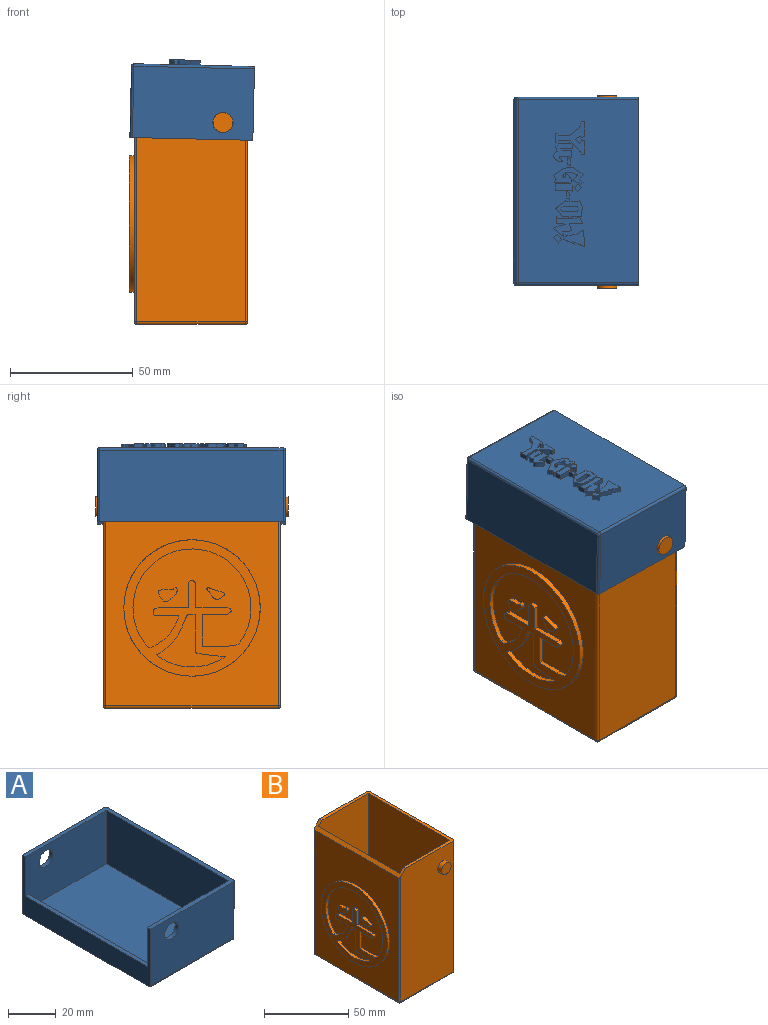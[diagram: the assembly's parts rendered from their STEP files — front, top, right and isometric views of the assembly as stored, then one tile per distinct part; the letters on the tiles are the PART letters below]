
ASSEMBLY  parts=2 mates=1
PART A: 165 faces, bbox 50x76.5x32 mm
  f0: plane 48x27.5mm, normal (0,1,0), area 1252.4mm2, adj f3,f7,f8,f9,f10,f163,f164
  f1: plane 48x27.5mm, normal (0,-1,0), area 1252.4mm2, adj f3,f7,f8,f9,f11,f163,f164
  f2: plane 74.5x49mm, normal (0,0,-1), area 3356mm2, adj f3,f13,f15,f16,f19,f20,f21,f22
  f3: plane 76.5x30mm, normal (-1,0,0), area 835.1mm2, adj f0,f1,f2,f4,f5,f7,f13,f16
  f4: plane 49x29mm, normal (0,1,0), area 1368.2mm2, adj f3,f7,f11,f12,f13
  f5: plane 49x29mm, normal (0,-1,0), area 1368.2mm2, adj f3,f7,f10,f16,f18
  f6: plane 74.5x29mm, normal (1,0,0), area 2160.5mm2, adj f7,f12,f15,f18
  f7: plane 76.5x50mm, normal (0,0,1), area 344.6mm2, adj f0,f1,f3,f4,f5,f6,f8,f12
  f8: plane 72.5x27.5mm, normal (-1,0,0), area 1993.7mm2, adj f0,f1,f7,f9
  f9: plane 72.5x46mm, normal (0,0,1), area 3335mm2, adj f0,f1,f8,f163
  f10: cylinder r=4.1mm len=8.2mm, axis (0,-1,0), area 51.5mm2, adj f0,f5
  f11: cylinder r=4.1mm len=8.2mm, axis (0,1,0), area 51.5mm2, adj f1,f4
  f12: cylinder r=1mm len=29mm, axis (0,0,-1), area 45.6mm2, adj f4,f6,f7,f14
  f13: cylinder r=1mm len=49mm, axis (-1,0,0), area 77mm2, adj f2,f3,f4,f14
  f14: sphere r=1mm, area 1.6mm2, adj f12,f13,f15
  f15: cylinder r=1mm len=74.5mm, axis (0,1,0), area 117mm2, adj f2,f6,f14,f17
  f16: cylinder r=1mm len=49mm, axis (1,0,0), area 77mm2, adj f2,f3,f5,f17
  f17: sphere r=1mm, area 1.6mm2, adj f15,f16,f18
  f18: cylinder r=1mm len=29mm, axis (0,0,1), area 45.6mm2, adj f5,f6,f7,f17
  f19: plane 2x1.25mm, normal (0.04,1,0), area 2.5mm2, adj f2,f20,f45,f46
  f20: plane 2x0.68mm, normal (0.84,0.54,0), area 1.6mm2, adj f2,f19,f21,f46
  f21: plane 2x0.63mm, normal (1,0,0), area 1.3mm2, adj f2,f20,f22,f46
  f22: plane 2x1.26mm, normal (0.91,0.42,0), area 2.8mm2, adj f2,f21,f23,f46
  f23: plane 3.69x3.04mm, normal (0.64,0.77,0), area 9.6mm2, adj f2,f22,f24,f46
  f24: plane 4.67x2mm, normal (0,1,0), area 9.3mm2, adj f2,f23,f25,f46
  f25: plane 2x0.69mm, normal (-0.81,0.58,0), area 1.7mm2, adj f2,f24,f26,f46
  f26: plane 2x0.42mm, normal (0,1,0), area 0.8mm2, adj f2,f25,f27,f46
  f27: plane 3.57x2mm, normal (1,0,0), area 7.1mm2, adj f2,f26,f28,f46
  f28: plane 2x0.42mm, normal (0,-1,0), area 0.8mm2, adj f2,f27,f29,f46
  f29: plane 2x0.73mm, normal (-0.84,-0.54,0), area 1.7mm2, adj f2,f28,f30,f46
  f30: plane 4.93x2mm, normal (0,-1,0), area 9.9mm2, adj f2,f29,f31,f46
  f31: plane 2x1.3mm, normal (0.72,-0.69,0), area 3.6mm2, adj f2,f30,f32,f46
  f32: plane 2x1.64mm, normal (0.72,-0.69,0), area 4.5mm2, adj f2,f31,f33,f46
  f33: plane 2x1.2mm, normal (0.69,-0.72,0), area 3.3mm2, adj f2,f32,f34,f46
  f34: plane 2x1.22mm, normal (0.94,-0.35,0), area 2.6mm2, adj f2,f33,f35,f46
  f35: plane 2x1.15mm, normal (0,-1,0), area 2.3mm2, adj f2,f34,f36,f46
  f36: plane 5.31x2mm, normal (-1,0,0), area 10.6mm2, adj f2,f35,f37,f46
  f37: plane 2x1.15mm, normal (-0.45,0.9,0), area 2.6mm2, adj f2,f36,f38,f46
  f38: plane 2x0.57mm, normal (1,0,0), area 1.1mm2, adj f2,f37,f39,f46
  f39: plane 2x0.84mm, normal (0.72,0.69,0), area 2.3mm2, adj f2,f38,f40,f46
  f40: plane 2x1.72mm, normal (-0.69,0.72,0), area 4.7mm2, adj f2,f39,f41,f46
  f41: plane 2x1.81mm, normal (-0.5,-0.87,0), area 4.2mm2, adj f2,f40,f42,f46
  f42: plane 2x0.31mm, normal (-0.48,-0.88,0), area 0.7mm2, adj f2,f41,f43,f46
  f43: plane 2x0.75mm, normal (0.88,-0.48,0), area 1.7mm2, adj f2,f42,f44,f46
  f44: plane 2x1.25mm, normal (-0.48,-0.88,0), area 2.8mm2, adj f2,f43,f45,f46
  f45: plane 5.87x2mm, normal (-1,0,0), area 11.7mm2, adj f2,f19,f44,f46
  f46: plane 13.11x11.53mm, normal (0,0,-1), area 53.7mm2, adj f19,f20,f21,f22,f23,f24,f25,f26
  f47: extruded ~3.74x3.36mm, area 16.8mm2, adj f2,f48,f61,f62
  f48: plane 4.09x2mm, normal (0,-1,0), area 8.2mm2, adj f2,f47,f49,f62
  f49: plane 2x0.48mm, normal (0.75,-0.66,0), area 1.3mm2, adj f2,f48,f50,f62
  f50: plane 2x0.44mm, normal (0,-1,0), area 0.9mm2, adj f2,f49,f51,f62
  f51: plane 2.96x2mm, normal (-1,0,0), area 5.9mm2, adj f2,f50,f52,f62
  f52: plane 3.77x2mm, normal (0,1,0), area 7.5mm2, adj f2,f51,f53,f62
  f53: plane 2x0.76mm, normal (-0.8,0.6,0), area 1.9mm2, adj f2,f52,f54,f62
  f54: plane 4.52x2mm, normal (0,-1,0), area 9mm2, adj f2,f53,f55,f62
  f55: plane 2x1.47mm, normal (-1,0,0), area 2.9mm2, adj f2,f54,f56,f62
  f56: plane 2x0.91mm, normal (-0.72,0.69,0), area 2.5mm2, adj f2,f55,f57,f62
  f57: plane 2x0.43mm, normal (1,0,0), area 0.9mm2, adj f2,f56,f58,f62
  f58: plane 4.58x2mm, normal (0,1,0), area 9.1mm2, adj f2,f57,f59,f62
  f59: plane 2x1.21mm, normal (0.69,0.72,0), area 3.4mm2, adj f2,f58,f60,f62
  f60: plane 2x1.84mm, normal (0.96,-0.29,0), area 3.9mm2, adj f2,f59,f61,f62
  f61: plane 2x1.07mm, normal (0.69,0.72,0), area 3mm2, adj f2,f47,f60,f62
  f62: plane 7.94x7.77mm, normal (0,0,-1), area 35.4mm2, adj f47,f48,f49,f50,f51,f52,f53,f54
  f63: plane 2x1.33mm, normal (-0.53,0.85,0), area 3.1mm2, adj f2,f64,f66,f67
  f64: plane 2.72x2mm, normal (1,0,0), area 5.4mm2, adj f2,f63,f65,f67
  f65: plane 2x1.33mm, normal (0.34,-0.94,0), area 2.8mm2, adj f2,f64,f66,f67
  f66: plane 2.36x2mm, normal (-1,0,0), area 4.7mm2, adj f2,f63,f65,f67
  f67: plane 3.19x1.33mm, normal (0,0,-1), area 3.4mm2, adj f63,f64,f65,f66
  f68: plane 2x0.41mm, normal (-0.52,-0.85,0), area 1mm2, adj f2,f69,f83,f84
  f69: extruded ~5.78x4.23mm, area 29.1mm2, adj f2,f68,f70,f84
  f70: plane 2x1.78mm, normal (0.81,0.58,0), area 4.4mm2, adj f2,f69,f71,f84
  f71: extruded ~3.12x2mm, area 7.1mm2, adj f2,f70,f72,f84
  f72: plane 2x0.93mm, normal (-0.7,-0.71,0), area 2.6mm2, adj f2,f71,f73,f84
  f73: plane 2x1.33mm, normal (-0.71,0.7,0), area 3.8mm2, adj f2,f72,f74,f84
  f74: plane 2x1.92mm, normal (-0.82,-0.57,0), area 4.7mm2, adj f2,f73,f75,f84
  f75: plane 4.23x2.91mm, normal (-0.57,0.82,0), area 10.3mm2, adj f2,f74,f76,f84
  f76: plane 2.1x2mm, normal (0,1,0), area 4.2mm2, adj f2,f75,f77,f84
  f77: plane 2x1.84mm, normal (0.4,0.91,0), area 4mm2, adj f2,f76,f78,f84
  f78: plane 3.84x2.34mm, normal (0.52,0.85,0), area 9mm2, adj f2,f77,f79,f84
  f79: plane 2x1.66mm, normal (0.85,-0.52,0), area 3.9mm2, adj f2,f78,f80,f84
  f80: plane 2x1.49mm, normal (0.91,0.4,0), area 3.3mm2, adj f2,f79,f81,f84
  f81: plane 5.87x2mm, normal (0,-1,0), area 11.7mm2, adj f2,f80,f82,f84
  f82: plane 2x0.38mm, normal (0.85,-0.52,0), area 0.9mm2, adj f2,f81,f83,f84
  f83: plane 2x0.49mm, normal (-0.26,-0.97,0), area 1mm2, adj f2,f68,f82,f84
  f84: plane 12.01x7.08mm, normal (0,0,-1), area 46.9mm2, adj f68,f69,f70,f71,f72,f73,f74,f75
  f85: plane 2x0.44mm, normal (0.26,0.97,0), area 0.9mm2, adj f2,f86,f96,f97
  f86: plane 4.56x2mm, normal (-0.01,1,0), area 9.1mm2, adj f2,f85,f87,f97
  f87: plane 2x0.48mm, normal (0,1,0), area 1mm2, adj f2,f86,f88,f97
  f88: plane 2.5x2mm, normal (1,0,0), area 5mm2, adj f2,f87,f89,f97
  f89: plane 5.77x2mm, normal (0,-1,0), area 11.5mm2, adj f2,f88,f90,f97
  f90: plane 2x0.85mm, normal (0.5,-0.87,0), area 2mm2, adj f2,f89,f91,f97
  f91: plane 2.48x2mm, normal (-1,0,0), area 5mm2, adj f2,f90,f92,f97
  f92: plane 2x0.72mm, normal (-0.76,0.65,0), area 1.9mm2, adj f2,f91,f93,f97
  f93: plane 2x0.02mm, normal (-0.11,0.99,0), area 0mm2, adj f2,f92,f94,f97
  f94: plane 2x0.4mm, normal (0.52,0.85,0), area 0.9mm2, adj f2,f93,f95,f97
  f95: plane 2x0.12mm, normal (-0.85,0.52,0), area 0.3mm2, adj f2,f94,f96,f97
  f96: plane 2x0.01mm, normal (-0.31,0.95,0), area 0mm2, adj f2,f85,f95,f97
  f97: plane 6.62x3.21mm, normal (0,0,-1), area 16.7mm2, adj f85,f86,f87,f88,f89,f90,f91,f92
  f98: plane 2x1.55mm, normal (0.79,0.62,0), area 3.9mm2, adj f2,f99,f101,f102
  f99: plane 2x1.39mm, normal (0.75,-0.66,0), area 3.7mm2, adj f2,f98,f100,f102
  f100: plane 2x1.8mm, normal (-0.66,-0.75,0), area 4.8mm2, adj f2,f99,f101,f102
  f101: plane 2x1.8mm, normal (-0.61,0.79,0), area 4.5mm2, adj f2,f98,f100,f102
  f102: plane 3.01x2.94mm, normal (0,0,-1), area 4.4mm2, adj f98,f99,f100,f101
  f103: plane 2x1.27mm, normal (-0.54,0.84,0), area 3mm2, adj f2,f104,f106,f107
  f104: plane 2.75x2mm, normal (1,0,0), area 5.5mm2, adj f2,f103,f105,f107
  f105: plane 2x1.27mm, normal (0.35,-0.94,0), area 2.7mm2, adj f2,f104,f106,f107
  f106: plane 2.41x2mm, normal (-1,0,0), area 4.8mm2, adj f2,f103,f105,f107
  f107: plane 3.23x1.27mm, normal (0,0,-1), area 3.3mm2, adj f103,f104,f105,f106
  f108: extruded ~6.71x2mm, area 16.4mm2, adj f2,f109,f127,f128
  f109: plane 2x0.63mm, normal (0.55,0.84,0), area 1.5mm2, adj f2,f108,f110,f128
  f110: plane 2.88x2mm, normal (0,1,0), area 5.8mm2, adj f2,f109,f111,f128
  f111: plane 2x0.78mm, normal (-0.53,0.85,0), area 1.9mm2, adj f2,f110,f112,f128
  f112: plane 2x0.47mm, normal (1,0,0), area 0.9mm2, adj f2,f111,f113,f128
  f113: plane 2x1.58mm, normal (0,1,0), area 3.2mm2, adj f2,f112,f114,f128
  f114: plane 2x0.27mm, normal (-1,0,0), area 0.5mm2, adj f2,f113,f115,f128
  f115: plane 3.79x3.07mm, normal (0.63,0.78,0), area 9.8mm2, adj f2,f114,f116,f128
  f116: plane 3.28x2.66mm, normal (0.78,-0.63,0), area 8.4mm2, adj f2,f115,f117,f128
  f117: plane 2.46x2mm, normal (0,-1,0), area 4.9mm2, adj f2,f116,f118,f128
  f118: plane 2x0.42mm, normal (1,0,0), area 0.8mm2, adj f2,f117,f119,f128
  f119: plane 2x0.73mm, normal (0,-1,0), area 1.5mm2, adj f2,f118,f120,f128
  f120: plane 2x0.52mm, normal (-0.66,-0.75,0), area 1.4mm2, adj f2,f119,f127,f128
  f121: plane 2x1.16mm, normal (0.94,-0.35,0), area 2.5mm2, adj f122,f126,f128,f129
  f122: plane 2x0.96mm, normal (0.91,0.41,0), area 2.1mm2, adj f121,f123,f128,f129
  f123: plane 5.92x2mm, normal (0,1,0), area 11.8mm2, adj f122,f124,f128,f129
  f124: plane 2x1.05mm, normal (-0.78,0.62,0), area 2.7mm2, adj f123,f125,f128,f129
  f125: plane 2x1.06mm, normal (-0.73,-0.69,0), area 2.9mm2, adj f124,f126,f128,f129
  f126: plane 5.75x2mm, normal (0,-1,0), area 11.5mm2, adj f121,f125,f128,f129
  f127: plane 2.73x2mm, normal (0,-1,0), area 5.5mm2, adj f2,f108,f120,f128
  f128: plane 10.89x6.97mm, normal (0,0,-1), area 40.5mm2, adj f108,f109,f110,f111,f112,f113,f114,f115
  f129: plane 7.18x2.11mm, normal (0,0,-1), area 13.8mm2, adj f121,f122,f123,f124,f125,f126
  f130: plane 2.54x2mm, normal (-0.91,0.43,0), area 5.6mm2, adj f2,f131,f145,f146
  f131: plane 2x1.04mm, normal (-0.03,1,0), area 2.1mm2, adj f2,f130,f132,f146
  f132: plane 2x0.47mm, normal (0.74,0.67,0), area 1.3mm2, adj f2,f131,f133,f146
  f133: plane 7.29x2mm, normal (0,1,0), area 14.6mm2, adj f2,f132,f134,f146
  f134: plane 2x0.84mm, normal (-0.71,0.71,0), area 2.4mm2, adj f2,f133,f135,f146
  f135: plane 2.94x2mm, normal (1,0,0), area 5.9mm2, adj f2,f134,f136,f146
  f136: plane 3.18x2mm, normal (0,-1,0), area 6.4mm2, adj f2,f135,f137,f146
  f137: plane 2x0.47mm, normal (0.69,-0.73,0), area 1.3mm2, adj f2,f136,f138,f146
  f138: plane 2.36x2mm, normal (0.17,0.99,0), area 4.8mm2, adj f2,f137,f139,f146
  f139: plane 2.42x2mm, normal (0.43,0.9,0), area 5.3mm2, adj f2,f138,f140,f146
  f140: plane 4.18x3.38mm, normal (0.63,-0.78,0), area 10.7mm2, adj f2,f139,f141,f146
  f141: plane 2x0.09mm, normal (-0.28,-0.96,0), area 0.2mm2, adj f2,f140,f142,f146
  f142: plane 2x1.91mm, normal (-0.96,0.28,0), area 4mm2, adj f2,f141,f143,f146
  f143: plane 3.62x2mm, normal (-0.14,-0.99,0), area 7.3mm2, adj f2,f142,f144,f146
  f144: plane 2.92x2mm, normal (-0.95,0.3,0), area 6.1mm2, adj f2,f143,f145,f146
  f145: plane 5.51x2mm, normal (0,-1,0), area 11mm2, adj f2,f130,f144,f146
  f146: plane 11.92x8.3mm, normal (0,0,-1), area 41.3mm2, adj f130,f131,f132,f133,f134,f135,f136,f137
  f147: plane 4.6x2.04mm, normal (0.41,-0.91,0), area 10.1mm2, adj f2,f148,f156,f157
  f148: plane 6.68x2mm, normal (-1,0.02,0), area 13.4mm2, adj f2,f147,f149,f157
  f149: plane 2.74x2mm, normal (0.48,0.88,0), area 6.3mm2, adj f2,f148,f150,f157
  f150: plane 3.25x2mm, normal (0.2,0.98,0), area 6.6mm2, adj f2,f149,f151,f157
  f151: plane 2x1.1mm, normal (0,1,0), area 2.2mm2, adj f2,f150,f152,f157
  f152: plane 2x0.47mm, normal (1,0,0), area 0.9mm2, adj f2,f151,f153,f157
  f153: plane 2x1.02mm, normal (0.15,0.99,0), area 2.1mm2, adj f2,f152,f154,f157
  f154: plane 2x1mm, normal (1,0,0), area 2mm2, adj f2,f153,f155,f157
  f155: plane 4.2x2mm, normal (0.41,-0.91,0), area 9.2mm2, adj f2,f154,f156,f157
  f156: plane 2x1mm, normal (-0.87,0.5,0), area 2.3mm2, adj f2,f147,f155,f157
  f157: plane 8.23x6.68mm, normal (0,0,-1), area 29.3mm2, adj f147,f148,f149,f150,f151,f152,f153,f154
  f158: plane 2.36x2mm, normal (-0.82,0.57,0), area 5.7mm2, adj f2,f159,f161,f162
  f159: plane 2x1.67mm, normal (0.66,0.75,0), area 4.5mm2, adj f2,f158,f160,f162
  f160: plane 2.14x2mm, normal (0.75,-0.66,0), area 5.7mm2, adj f2,f159,f161,f162
  f161: plane 2x1.42mm, normal (-0.66,-0.75,0), area 3.8mm2, adj f2,f158,f160,f162
  f162: plane 3.61x3.3mm, normal (0,0,-1), area 5.9mm2, adj f158,f159,f160,f161
  f163: plane 72.5x7.37mm, normal (1,0,0), area 534.3mm2, adj f0,f1,f9,f164
  f164: plane 72.5x2mm, normal (0,0,1), area 145mm2, adj f0,f1,f3,f163
PART B: 55 faces, bbox 48x78.4x96 mm
  f0: plane 90x70mm, normal (-1,0,0), area 3885.8mm2, adj f15,f18,f24,f27,f47
  f1: plane 72x41mm, normal (0,0,1), area 299.6mm2, adj f2,f3,f4,f6,f8,f9,f15,f16
  f2: plane 95x44mm, normal (0,1,0), area 4121.7mm2, adj f1,f13,f15,f21,f25,f27
  f3: plane 95x44mm, normal (0,-1,0), area 4121.7mm2, adj f1,f11,f15,f16,f18,f19
  f4: plane 95x70mm, normal (1,0,0), area 6650mm2, adj f1,f16,f20,f21
  f5: plane 70x44mm, normal (0,0,-1), area 3080mm2, adj f19,f20,f24,f25
  f6: plane 92x42mm, normal (0,-1,0), area 3859.5mm2, adj f1,f7,f9,f10,f15
  f7: plane 89x68mm, normal (1,0,0), area 6052mm2, adj f6,f8,f10,f15
  f8: plane 92x42mm, normal (0,1,0), area 3859.5mm2, adj f1,f7,f9,f10,f15
  f9: plane 92x68mm, normal (-1,0,0), area 6256mm2, adj f1,f6,f8,f10
  f10: plane 68x42mm, normal (0,0,1), area 2856mm2, adj f6,f7,f8,f9
  f11: cylinder r=4mm len=8mm, axis (0,1,0), area 80.4mm2, adj f3,f12
  f12: plane 8x8mm, normal (0,-1,0), area 50.3mm2, adj f11
  f13: cylinder r=4mm len=8mm, axis (0,-1,0), area 80.4mm2, adj f2,f14
  f14: plane 8x8mm, normal (0,1,0), area 50.3mm2, adj f13
  f15: plane 72x5mm, normal (-0.71,0,0.71), area 220mm2, adj f0,f1,f2,f3,f6,f7,f8,f18
  f16: cylinder r=1mm len=95mm, axis (0,0,1), area 149.2mm2, adj f1,f3,f4,f17
  f17: sphere r=1mm, area 1.6mm2, adj f16,f19,f20
  f18: cylinder r=1mm len=91mm, axis (0,0,-1), area 141.9mm2, adj f0,f3,f15,f22
  f19: cylinder r=1mm len=44mm, axis (1,0,0), area 69.1mm2, adj f3,f5,f17,f22
  f20: cylinder r=1mm len=70mm, axis (0,1,0), area 110mm2, adj f4,f5,f17,f23
  f21: cylinder r=1mm len=95mm, axis (0,0,-1), area 149.2mm2, adj f1,f2,f4,f23
  f22: sphere r=1mm, area 1.6mm2, adj f18,f19,f24
  f23: sphere r=1mm, area 1.6mm2, adj f20,f21,f25
  f24: cylinder r=1mm len=70mm, axis (0,-1,0), area 110mm2, adj f0,f5,f22,f26
  f25: cylinder r=1mm len=44mm, axis (-1,0,0), area 69.1mm2, adj f2,f5,f23,f26
  f26: sphere r=1mm, area 1.6mm2, adj f24,f25,f27
  f27: cylinder r=1mm len=91mm, axis (0,0,1), area 141.9mm2, adj f0,f2,f15,f26
  f28: cylinder r=24mm len=48mm, axis (1,0,0), area 217.9mm2, adj f29,f45,f48,f54
  f29: extruded ~4.42x2mm, area 9mm2, adj f28,f30,f48,f54
  f30: plane 10.2x2mm, normal (0,0,1), area 20.4mm2, adj f29,f31,f48,f54
  f31: plane 12.82x2mm, normal (0,-1,0), area 25.6mm2, adj f30,f32,f48,f54
  f32: plane 10.2x2mm, normal (0,0,-1), area 20.4mm2, adj f31,f33,f48,f54
  f33: extruded ~2.71x2mm, area 8.3mm2, adj f32,f34,f48,f54
  f34: plane 12.92x2mm, normal (0,0,1), area 25.8mm2, adj f33,f35,f48,f54
  f35: plane 10.25x2mm, normal (0,-1,0), area 20.5mm2, adj f34,f36,f48,f54
  f36: extruded ~3.07x2mm, area 7.3mm2, adj f35,f37,f48,f54
  f37: plane 10.25x2mm, normal (0,1,0), area 20.5mm2, adj f36,f38,f48,f54
  f38: plane 12.32x2mm, normal (0,0,1), area 24.6mm2, adj f37,f39,f48,f54
  f39: extruded ~3.27x2mm, area 11.8mm2, adj f38,f40,f48,f54
  f40: plane 7.99x2mm, normal (0,0,-1), area 16mm2, adj f39,f45,f48,f54
  f41: cylinder r=24mm len=28.1mm, axis (1,0,0), area 60.1mm2, adj f42,f46,f48,f49
  f42: extruded ~16.38x13.14mm, area 43.4mm2, adj f41,f43,f48,f49
  f43: plane 2.71x2mm, normal (0,0,-1), area 5.4mm2, adj f42,f44,f48,f49
  f44: plane 14.58x2mm, normal (0,1,0), area 29.2mm2, adj f43,f46,f48,f49
  f45: extruded ~13.01x12.43mm, area 38.8mm2, adj f28,f40,f48,f54
  f46: extruded ~12.25x2.52mm, area 26.2mm2, adj f41,f44,f48,f49
  f47: cylinder r=27.72mm len=55.44mm, axis (1,0,0), area 348.4mm2, adj f0,f48
  f48: plane 55.44x55.44mm, normal (-1,0,0), area 885.4mm2, adj f28,f29,f30,f31,f32,f33,f34,f35
  f49: plane 28.28x21.29mm, normal (-1,0,0), area 223.1mm2, adj f41,f42,f43,f44,f46
  f50: plane 7.93x6.13mm, normal (-1,0,0), area 26.7mm2, adj f52
  f51: plane 7.41x4.99mm, normal (-1,0,0), area 18.5mm2, adj f53
  f52: extruded ~7.59x5.8mm, area 42.2mm2, adj f50,f54
  f53: extruded ~7.16x4.75mm, area 36.4mm2, adj f51,f54
  f54: plane 48x40.14mm, normal (-1,0,0), area 1260.5mm2, adj f28,f29,f30,f31,f32,f33,f34,f35
PLACE A rot(axis=(0,-1,0),178.7deg) t=(111.8,16.95,104.89)mm
PLACE B t=(110.97,16.7,-0.5)mm fixed
MATE revolute B.f11 <-> A.f10  axis (0,-1,0) through (123.97,-19.3,81.5)mm
